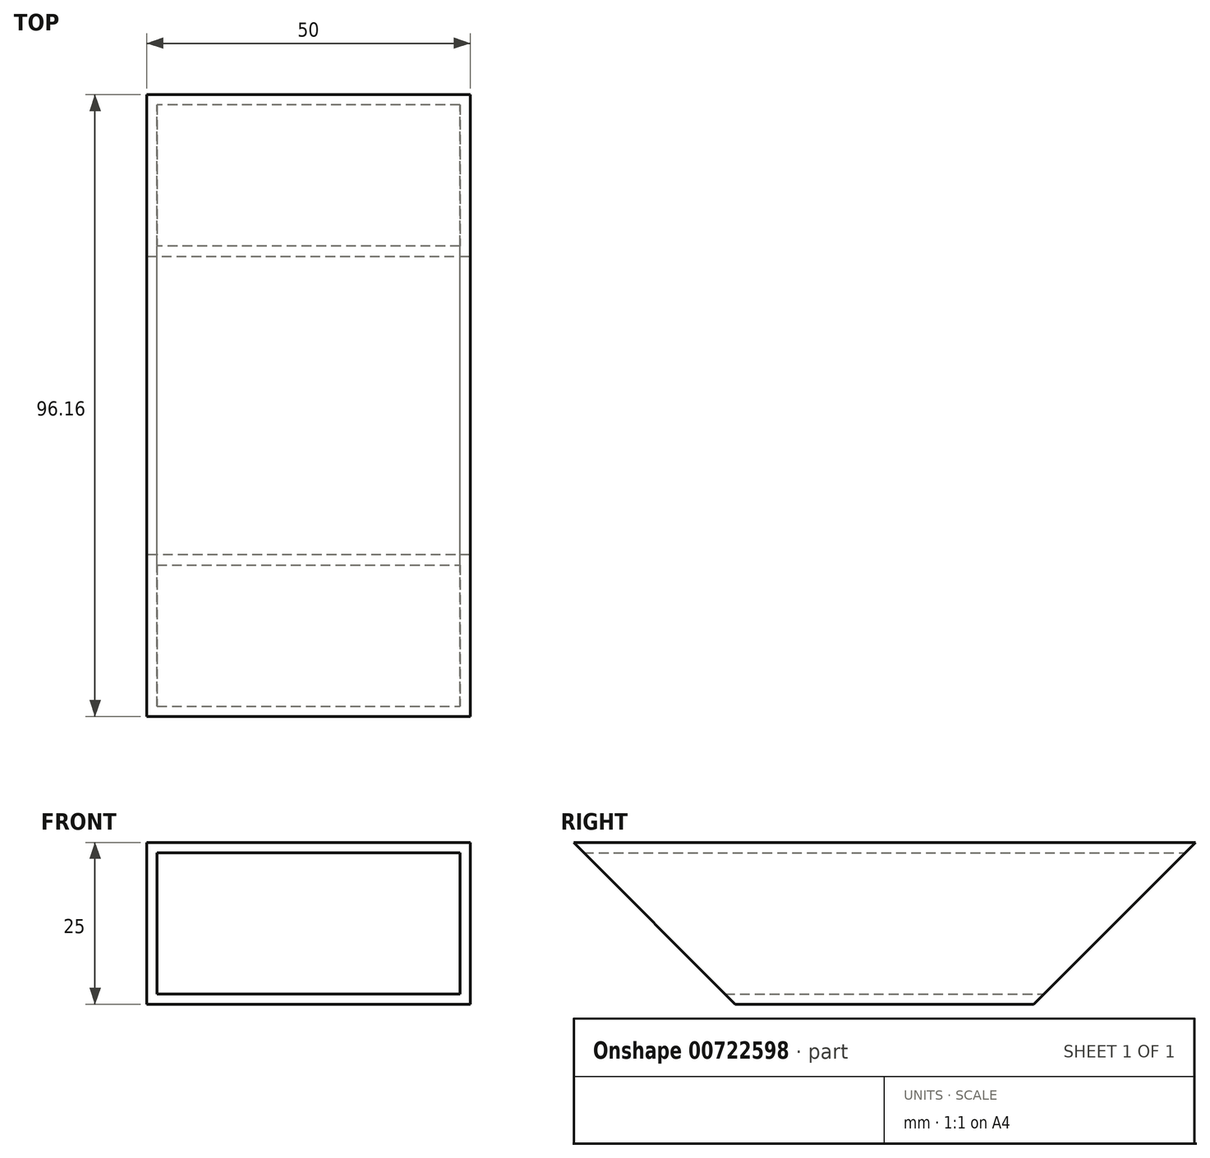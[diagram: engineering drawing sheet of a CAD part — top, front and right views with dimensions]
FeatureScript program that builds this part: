
annotation { "Feature Type Name" : "Feature", "Feature Type Description" : "" }
export const myFeature = defineFeature(function(context is Context, id is Id, definition is map)
    precondition{}
    {
        {
            var Q0;
            Q0=qCreatedBy(makeId("Front.planeOp"),FACE);
            var sketch = newSketch(context, id + "F0", { "sketchPlane" : qUnion([Q0])});
            skLineSegment(sketch, "E0.bottom", {"start": v(-25, -12.5) * mm, "end": v(25, -12.5) * mm});
            skLineSegment(sketch, "E0.top", {"start": v(-25, 12.5) * mm, "end": v(25, 12.5) * mm});
            skLineSegment(sketch, "E0.left", {"start": v(-25, -12.5) * mm, "end": v(-25, 12.5) * mm});
            skLineSegment(sketch, "E0.right", {"start": v(25, -12.5) * mm, "end": v(25, 12.5) * mm});
            skPoint(sketch, "E0.middle", {"position": v(0, 0) * mm});
            skLineSegment(sketch, "E1.bottom", {"start": v(-23.41, -10.91) * mm, "end": v(23.41, -10.91) * mm});
            skLineSegment(sketch, "E1.top", {"start": v(-23.41, 10.91) * mm, "end": v(23.41, 10.91) * mm});
            skLineSegment(sketch, "E1.left", {"start": v(-23.41, -10.91) * mm, "end": v(-23.41, 10.91) * mm});
            skLineSegment(sketch, "E1.right", {"start": v(23.41, -10.91) * mm, "end": v(23.41, 10.92) * mm});
            skSolve(sketch);
        }
        {
            var Q0;
            Q0=makeQuery(id+"F0.imprint","IMPRINT",FACE,{"disambiguationData":[TD([[makeQuery(id+"F0.imprint","IMPRINT",EDGE,{"derivedFrom":sQuery(id+"F0.wireOp",EDGE,"E0.bottom")}),1.0]])]});
            extrude(context, id + "F1", {"entities" : qUnion([Q0]), "endBound" : BoundingType.SYMMETRIC, "depth" : 96.16 * mm, "offsetDistance" : 25 * mm});
        }
        {
            var Q0;
            Q0=makeQuery(id+"F1.opExtrude","CAP_EDGE",EDGE,{"disambiguationData":[OSD([sQuery(id+"F0.wireOp",EDGE,"E0.bottom")])],"isStart":false});
            chamfer(context, id + "F2", {"entities" : qUnion([Q0]), "width" : 25 * mm, "tangentPropagation" : true});
        }
        {
            var Q0;
            Q0=makeQuery(id+"F1.opExtrude","CAP_EDGE",EDGE,{"disambiguationData":[OSD([sQuery(id+"F0.wireOp",EDGE,"E0.bottom")])],"isStart":true});
            chamfer(context, id + "F3", {"entities" : qUnion([Q0]), "width" : 25 * mm, "tangentPropagation" : true});
        }
    });
